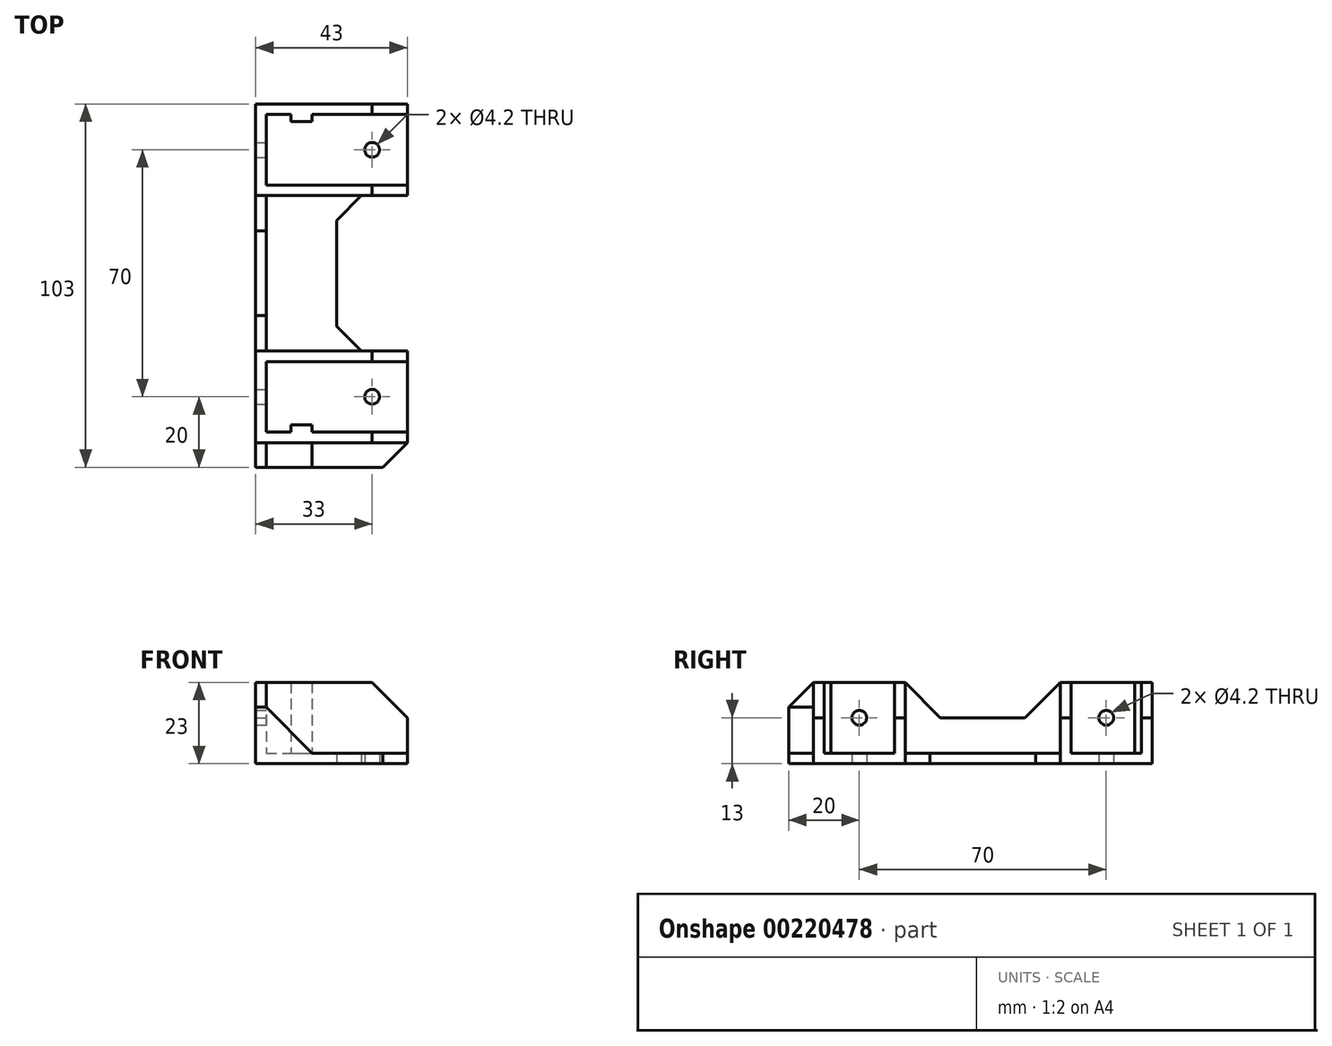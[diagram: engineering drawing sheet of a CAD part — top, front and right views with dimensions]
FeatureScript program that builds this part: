
annotation { "Feature Type Name" : "Feature", "Feature Type Description" : "" }
export const myFeature = defineFeature(function(context is Context, id is Id, definition is map)
    precondition{}
    {
        {
            var Q0;
            Q0=qCreatedBy(makeId("Top.planeOp"),FACE);
            var sketch = newSketch(context, id + "F0", { "sketchPlane" : qUnion([Q0])});
            skLineSegment(sketch, "E0.bottom", {"start": v(0, 0) * mm, "end": v(40, 0) * mm, "construction": true});
            skLineSegment(sketch, "E0.top", {"start": v(0, 20) * mm, "end": v(40, 20) * mm, "construction": true});
            skLineSegment(sketch, "E0.left", {"start": v(0, 0) * mm, "end": v(0, 20) * mm, "construction": true});
            skLineSegment(sketch, "E0.right", {"start": v(40, 0) * mm, "end": v(40, 20) * mm, "construction": true});
            skLineSegment(sketch, "E1.bottom", {"start": v(0, 70) * mm, "end": v(40, 70) * mm, "construction": true});
            skLineSegment(sketch, "E1.top", {"start": v(0, 90) * mm, "end": v(40, 90) * mm, "construction": true});
            skLineSegment(sketch, "E1.left", {"start": v(0, 70) * mm, "end": v(0, 90) * mm, "construction": true});
            skLineSegment(sketch, "E1.right", {"start": v(40, 70) * mm, "end": v(40, 90) * mm, "construction": true});
            skLineSegment(sketch, "E2", {"start": v(40, 93) * mm, "end": v(40, 67) * mm});
            skLineSegment(sketch, "E3", {"start": v(40, 67) * mm, "end": v(27, 67) * mm});
            skLineSegment(sketch, "E4", {"start": v(27, 67) * mm, "end": v(20, 60) * mm});
            skLineSegment(sketch, "E5", {"start": v(20, 60) * mm, "end": v(20, 30) * mm});
            skLineSegment(sketch, "E6", {"start": v(20, 30) * mm, "end": v(27, 23) * mm});
            skLineSegment(sketch, "E7", {"start": v(27, 23) * mm, "end": v(40, 23) * mm});
            skLineSegment(sketch, "E8", {"start": v(40, 23) * mm, "end": v(40, -3) * mm});
            skLineSegment(sketch, "E9", {"start": v(40, -3) * mm, "end": v(33, -10) * mm});
            skLineSegment(sketch, "E10", {"start": v(33, -10) * mm, "end": v(-3, -10) * mm});
            skLineSegment(sketch, "E11", {"start": v(-3, -10) * mm, "end": v(-3, 93) * mm});
            skLineSegment(sketch, "E12", {"start": v(-3, 93) * mm, "end": v(40, 93) * mm});
            skPoint(sketch, "E13", {"position": v(40, 10) * mm});
            skPoint(sketch, "E14", {"position": v(40, 80) * mm});
            skPoint(sketch, "E14.positionSnap0", {"position": v(40, 80) * mm});
            skLineSegment(sketch, "E15", {"start": v(40, 90) * mm, "end": v(20, 70) * mm, "construction": true});
            skLineSegment(sketch, "E16", {"start": v(40, 20) * mm, "end": v(20, 0) * mm, "construction": true});
            skCircle(sketch, "E17", {"center": v(30, 10) * mm, "radius": 2.1 * mm});
            skCircle(sketch, "E18", {"center": v(30, 80) * mm, "radius": 2.1 * mm});
            skSolve(sketch);
        }
        {
            var Q0;
            Q0 = qSketchRegion(id + "F0", true);
            extrude(context, id + "F1", {"entities" : qUnion([Q0]), "depth" : 3 * mm});
        }
        {
            var Q0;
            Q0=makeQuery(id+"F1.opExtrude","CAP_FACE",FACE,{"disambiguationData":[OSD([sQuery(id+"F0.wireOp",EDGE,"E2"),sQuery(id+"F0.wireOp",EDGE,"E3"),sQuery(id+"F0.wireOp",EDGE,"E4"),sQuery(id+"F0.wireOp",EDGE,"E5"),sQuery(id+"F0.wireOp",EDGE,"E6"),sQuery(id+"F0.wireOp",EDGE,"E7"),sQuery(id+"F0.wireOp",EDGE,"E8"),sQuery(id+"F0.wireOp",EDGE,"E9"),sQuery(id+"F0.wireOp",EDGE,"E10"),sQuery(id+"F0.wireOp",EDGE,"E11"),sQuery(id+"F0.wireOp",EDGE,"E12"),sQuery(id+"F0.wireOp",EDGE,"E17"),sQuery(id+"F0.wireOp",EDGE,"E18")])],"isStart":false});
            var sketch = newSketch(context, id + "F2", { "sketchPlane" : qUnion([Q0])});
            skLineSegment(sketch, "E19", {"start": v(40, 93) * mm, "end": v(-3, 93) * mm});
            skLineSegment(sketch, "E20", {"start": v(-3, 93) * mm, "end": v(-3, -10) * mm});
            skLineSegment(sketch, "E21", {"start": v(-3, -10) * mm, "end": v(0, -10) * mm});
            skLineSegment(sketch, "E22", {"start": v(0, -10) * mm, "end": v(0, -3) * mm});
            skLineSegment(sketch, "E23", {"start": v(0, -3) * mm, "end": v(40, -3) * mm});
            skLineSegment(sketch, "E24", {"start": v(40, -3) * mm, "end": v(40, 0) * mm});
            skLineSegment(sketch, "E25", {"start": v(0, 0) * mm, "end": v(0, 20) * mm});
            skLineSegment(sketch, "E26", {"start": v(0, 20) * mm, "end": v(40, 20) * mm});
            skLineSegment(sketch, "E27", {"start": v(40, 20) * mm, "end": v(40, 23) * mm});
            skLineSegment(sketch, "E28", {"start": v(40, 23) * mm, "end": v(0, 23) * mm});
            skLineSegment(sketch, "E29", {"start": v(0, 23) * mm, "end": v(0, 67) * mm});
            skLineSegment(sketch, "E30", {"start": v(0, 67) * mm, "end": v(40, 67) * mm});
            skLineSegment(sketch, "E31", {"start": v(40, 67) * mm, "end": v(40, 70) * mm});
            skLineSegment(sketch, "E32", {"start": v(40, 70) * mm, "end": v(0, 70) * mm});
            skLineSegment(sketch, "E33", {"start": v(0, 70) * mm, "end": v(0, 90) * mm});
            skLineSegment(sketch, "E34", {"start": v(0, 90) * mm, "end": v(7, 90) * mm});
            skLineSegment(sketch, "E35", {"start": v(7, 90) * mm, "end": v(7, 88) * mm});
            skLineSegment(sketch, "E36", {"start": v(7, 88) * mm, "end": v(13, 88) * mm});
            skLineSegment(sketch, "E37", {"start": v(13, 88) * mm, "end": v(13, 90) * mm});
            skLineSegment(sketch, "E38", {"start": v(13, 90) * mm, "end": v(40, 90) * mm});
            skLineSegment(sketch, "E39", {"start": v(40, 90) * mm, "end": v(40, 93) * mm});
            skLineSegment(sketch, "E40", {"start": v(0, 0) * mm, "end": v(7, 0) * mm});
            skLineSegment(sketch, "E41", {"start": v(7, 0) * mm, "end": v(7, 2) * mm});
            skLineSegment(sketch, "E42", {"start": v(7, 2) * mm, "end": v(13, 2) * mm});
            skLineSegment(sketch, "E43", {"start": v(13, 2) * mm, "end": v(13, 0) * mm});
            skLineSegment(sketch, "E44", {"start": v(13, 0) * mm, "end": v(40, 0) * mm});
            skSolve(sketch);
        }
        {
            var Q0;
            Q0 = qSketchRegion(id + "F2", true);
            extrude(context, id + "F3", {"entities" : qUnion([Q0]), "operationType" : NewBodyOperationType.ADD, "depth" : 20 * mm});
        }
        {
            var Q0;
            Q0=makeQuery(id+"F3.opExtrude","SWEPT_FACE",FACE,{"disambiguationData":[OSD([sQuery(id+"F2.wireOp",EDGE,"E29")])]});
            var sketch = newSketch(context, id + "F4", { "sketchPlane" : qUnion([Q0])});
            skLineSegment(sketch, "E45", {"start": v(0, 23) * mm, "end": v(20, 3) * mm, "construction": true});
            skCircle(sketch, "E46", {"center": v(10, 13) * mm, "radius": 2.1 * mm});
            skLineSegment(sketch, "E47", {"start": v(23, 23) * mm, "end": v(33, 13) * mm});
            skPoint(sketch, "E47.endSnap0", {"position": v(23, 13) * mm});
            skLineSegment(sketch, "E48", {"start": v(33, 13) * mm, "end": v(57, 13) * mm});
            skLineSegment(sketch, "E49", {"start": v(57, 13) * mm, "end": v(67, 23) * mm});
            skLineSegment(sketch, "E50", {"start": v(67, 23) * mm, "end": v(23, 23) * mm});
            skLineSegment(sketch, "E51.0", {"start": v(70, 3) * mm, "end": v(90, 3) * mm, "construction": true});
            skLineSegment(sketch, "E52", {"start": v(70, 3) * mm, "end": v(90, 23) * mm, "construction": true});
            skLineSegment(sketch, "E53.0", {"start": v(0, 3) * mm, "end": v(20, 3) * mm, "construction": true});
            skCircle(sketch, "E54", {"center": v(80, 13) * mm, "radius": 2.1 * mm});
            skLineSegment(sketch, "E55.0", {"start": v(-10, 23) * mm, "end": v(-3, 23) * mm, "construction": true});
            skLineSegment(sketch, "E56", {"start": v(-3, 23) * mm, "end": v(-10, 23) * mm});
            skLineSegment(sketch, "E57", {"start": v(-10, 16) * mm, "end": v(-3, 23) * mm});
            skLineSegment(sketch, "E58", {"start": v(-10, 23) * mm, "end": v(-10, 16) * mm});
            skSolve(sketch);
        }
        {
            var Q0;
            Q0 = qSketchRegion(id + "F4", true);
            extrude(context, id + "F5", {"entities" : qUnion([Q0]), "operationType" : NewBodyOperationType.REMOVE, "endBound" : BoundingType.UP_TO_NEXT, "oppositeDirection" : true, "depth" : 25 * mm});
        }
        {
            var Q0;
            Q0=makeQuery(id+"F3.boolean.opBoolean","MERGE",FACE,{"derivedFrom":[makeQuery(id+"F1.opExtrude","SWEPT_FACE",FACE,{"disambiguationData":[OSD([sQuery(id+"F0.wireOp",EDGE,"E10")])]}),makeQuery(id+"F3.opExtrude","SWEPT_FACE",FACE,{"disambiguationData":[OSD([sQuery(id+"F2.wireOp",EDGE,"E21")])]})]});
            var sketch = newSketch(context, id + "F6", { "sketchPlane" : qUnion([Q0])});
            skLineSegment(sketch, "E59", {"start": v(0, 3) * mm, "end": v(0, 16) * mm});
            skLineSegment(sketch, "E60", {"start": v(0, 16) * mm, "end": v(13, 3) * mm});
            skLineSegment(sketch, "E61", {"start": v(13, 3) * mm, "end": v(0, 3) * mm});
            skSolve(sketch);
        }
        {
            var Q0;
            Q0=makeQuery(id+"F6.imprint","IMPRINT",FACE,{"disambiguationData":[TD([[makeQuery(id+"F6.imprint","IMPRINT",EDGE,{"derivedFrom":sQuery(id+"F6.wireOp",EDGE,"E59")}),1.0]])]});
            extrude(context, id + "F7", {"entities" : qUnion([Q0]), "operationType" : NewBodyOperationType.ADD, "endBound" : BoundingType.UP_TO_NEXT, "oppositeDirection" : true, "depth" : 25 * mm});
        }
        {
            var Q0;
            Q0=makeQuery(id+"F3.boolean.opBoolean","MERGE",FACE,{"derivedFrom":[makeQuery(id+"F1.opExtrude","SWEPT_FACE",FACE,{"disambiguationData":[OSD([sQuery(id+"F0.wireOp",EDGE,"E12")])]}),makeQuery(id+"F3.opExtrude","SWEPT_FACE",FACE,{"disambiguationData":[OSD([sQuery(id+"F2.wireOp",EDGE,"E19")])]})]});
            var sketch = newSketch(context, id + "F8", { "sketchPlane" : qUnion([Q0])});
            skLineSegment(sketch, "E62", {"start": v(-40, 23) * mm, "end": v(-30, 23) * mm});
            skLineSegment(sketch, "E63", {"start": v(-30, 23) * mm, "end": v(-40, 13) * mm});
            skLineSegment(sketch, "E64", {"start": v(-40, 13) * mm, "end": v(-40, 23) * mm});
            skSolve(sketch);
        }
        {
            var Q0;
            Q0=makeQuery(id+"F8.imprint","IMPRINT",FACE,{"disambiguationData":[TD([[makeQuery(id+"F8.imprint","IMPRINT",EDGE,{"derivedFrom":sQuery(id+"F8.wireOp",EDGE,"E62")}),1.0]])]});
            extrude(context, id + "F9", {"entities" : qUnion([Q0]), "operationType" : NewBodyOperationType.REMOVE, "endBound" : BoundingType.THROUGH_ALL, "oppositeDirection" : true, "depth" : 25 * mm});
        }
    });
